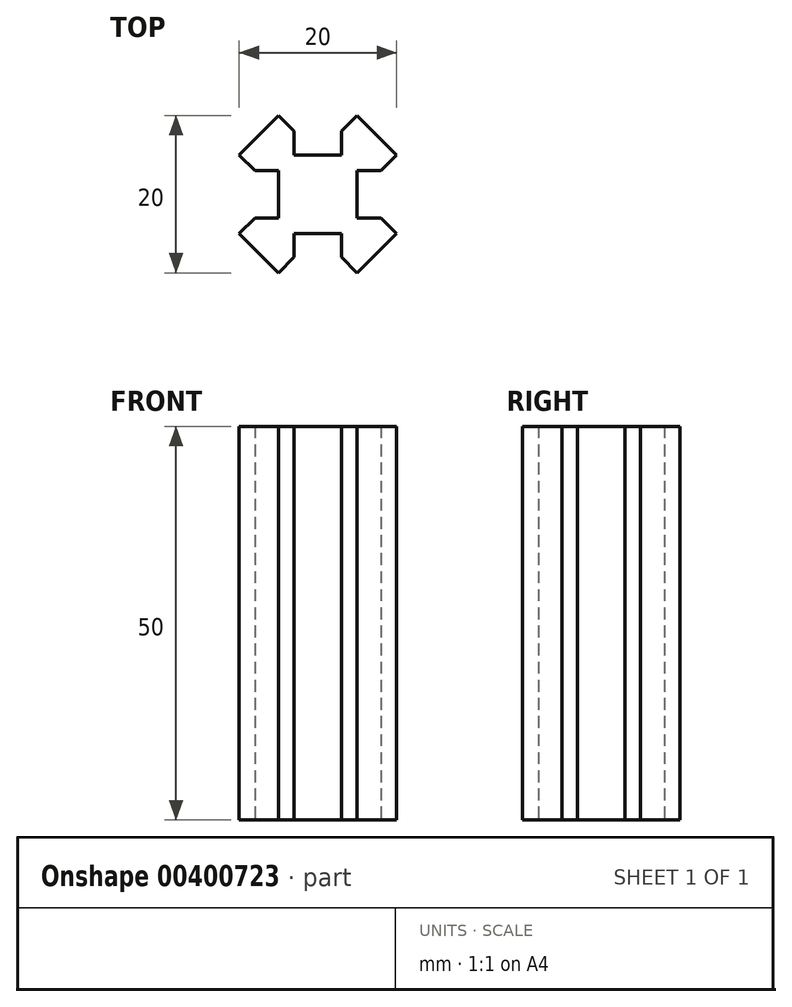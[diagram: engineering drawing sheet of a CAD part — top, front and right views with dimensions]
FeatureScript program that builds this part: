
annotation { "Feature Type Name" : "Feature", "Feature Type Description" : "" }
export const myFeature = defineFeature(function(context is Context, id is Id, definition is map)
    precondition{}
    {
        {
            var Q0;
            Q0=qCreatedBy(makeId("Top.planeOp"),FACE);
            var sketch = newSketch(context, id + "F0", { "sketchPlane" : qUnion([Q0])});
            skLineSegment(sketch, "E0.bottom", {"start": v(10, 10) * mm, "end": v(-10, 10) * mm});
            skLineSegment(sketch, "E0.top", {"start": v(10, -10) * mm, "end": v(-10, -10) * mm});
            skLineSegment(sketch, "E0.left", {"start": v(10, 10) * mm, "end": v(10, -10) * mm});
            skLineSegment(sketch, "E0.right", {"start": v(-10, 10) * mm, "end": v(-10, -10) * mm});
            skPoint(sketch, "E0.middle", {"position": v(0, 0) * mm});
            skLineSegment(sketch, "E1.bottom", {"start": v(5, -5) * mm, "end": v(-5, -5) * mm});
            skLineSegment(sketch, "E1.top", {"start": v(5, 5) * mm, "end": v(-5, 5) * mm});
            skLineSegment(sketch, "E1.left", {"start": v(5, -5) * mm, "end": v(5, 5) * mm});
            skLineSegment(sketch, "E1.right", {"start": v(-5, -5) * mm, "end": v(-5, 5) * mm});
            skLineSegment(sketch, "E2", {"start": v(10, -10) * mm, "end": v(10, -5) * mm});
            skLineSegment(sketch, "E3", {"start": v(10, -10) * mm, "end": v(5, -10) * mm});
            skLineSegment(sketch, "E4", {"start": v(5, -10) * mm, "end": v(3, -8) * mm});
            skLineSegment(sketch, "E5", {"start": v(10, -5) * mm, "end": v(8, -3) * mm});
            skLineSegment(sketch, "E6.top", {"start": v(10, 10) * mm, "end": v(10, 5) * mm});
            skLineSegment(sketch, "E6.left", {"start": v(5, 10) * mm, "end": v(10, 10) * mm});
            skLineSegment(sketch, "E7", {"start": v(10, 10) * mm, "end": v(5, 10) * mm});
            skLineSegment(sketch, "E8", {"start": v(10, 5) * mm, "end": v(8, 3) * mm});
            skLineSegment(sketch, "E9", {"start": v(5, 10) * mm, "end": v(3, 8) * mm});
            skLineSegment(sketch, "E10.top", {"start": v(-10, -10) * mm, "end": v(-10, -5) * mm});
            skLineSegment(sketch, "E10.left", {"start": v(-5, -10) * mm, "end": v(-10, -10) * mm});
            skLineSegment(sketch, "E11", {"start": v(-10, -10) * mm, "end": v(-5, -10) * mm});
            skLineSegment(sketch, "E12", {"start": v(-10, -5) * mm, "end": v(-8, -3) * mm});
            skLineSegment(sketch, "E13", {"start": v(-5, -10) * mm, "end": v(-3, -8) * mm});
            skLineSegment(sketch, "E14.top", {"start": v(-10, 10) * mm, "end": v(-5, 10) * mm});
            skLineSegment(sketch, "E14.left", {"start": v(-10, 5) * mm, "end": v(-10, 10) * mm});
            skLineSegment(sketch, "E15", {"start": v(-10, 10) * mm, "end": v(-10, 5) * mm});
            skLineSegment(sketch, "E16", {"start": v(-5, 10) * mm, "end": v(-3, 8) * mm});
            skLineSegment(sketch, "E17", {"start": v(-10, 5) * mm, "end": v(-8, 3) * mm});
            skLineSegment(sketch, "E18", {"start": v(-10, 5) * mm, "end": v(-5, 10) * mm});
            skLineSegment(sketch, "E19", {"start": v(5, 10) * mm, "end": v(10, 5) * mm});
            skLineSegment(sketch, "E20", {"start": v(5, -10) * mm, "end": v(10, -5) * mm});
            skLineSegment(sketch, "E21", {"start": v(-10, -5) * mm, "end": v(-5, -10) * mm});
            skLineSegment(sketch, "E22", {"start": v(-8, -3) * mm, "end": v(-5, -3) * mm});
            skLineSegment(sketch, "E23", {"start": v(-8, 3) * mm, "end": v(-5, 3) * mm});
            skPoint(sketch, "E23.endSnap0", {"position": v(-5, 0) * mm});
            skLineSegment(sketch, "E24", {"start": v(-3, 8) * mm, "end": v(-3, 5) * mm});
            skLineSegment(sketch, "E25", {"start": v(3, 8) * mm, "end": v(3, 5) * mm});
            skLineSegment(sketch, "E26", {"start": v(8, 3) * mm, "end": v(5, 3) * mm});
            skLineSegment(sketch, "E27", {"start": v(8, -3) * mm, "end": v(5, -3) * mm});
            skLineSegment(sketch, "E28", {"start": v(3, -8) * mm, "end": v(3, -5) * mm});
            skLineSegment(sketch, "E29", {"start": v(-3, -8) * mm, "end": v(-3, -5) * mm});
            skSolve(sketch);
        }
        {
            var Q0;
            Q0=makeQuery(id+"F0.imprint","IMPRINT",FACE,{"disambiguationData":[TD([[makeQuery(id+"F0.imprint","IMPRINT",EDGE,{"derivedFrom":sQuery(id+"F0.wireOp",EDGE,"E16")}),-1.0]])]});
            var Q1;
            {var subQ1=sQuery(id+"F0.wireOp",EDGE,"E1.bottom");var subQ4=sQuery(id+"F0.wireOp",EDGE,"E1.left");var subQ9=makeQuery(id+"F0.imprint","INTERSECT",VERTEX,{"derivedFrom":[subQ1,subQ4]});Q1=makeQuery(id+"F0.imprint","IMPRINT",FACE,{"disambiguationData":[TD([[makeQuery(id+"F0.imprint","IMPRINT",EDGE,{"disambiguationData":[TD([[subQ9,-1.0]])],"derivedFrom":subQ1}),-1.0]])]});}
            var Q2;
            Q2=makeQuery(id+"F0.imprint","IMPRINT",FACE,{"disambiguationData":[TD([[makeQuery(id+"F0.imprint","IMPRINT",EDGE,{"derivedFrom":sQuery(id+"F0.wireOp",EDGE,"E8")}),-1.0]])]});
            var Q3;
            Q3=makeQuery(id+"F0.imprint","IMPRINT",FACE,{"disambiguationData":[TD([[makeQuery(id+"F0.imprint","IMPRINT",EDGE,{"derivedFrom":sQuery(id+"F0.wireOp",EDGE,"E4")}),-1.0]])]});
            var Q4;
            Q4=makeQuery(id+"F0.imprint","IMPRINT",FACE,{"disambiguationData":[TD([[makeQuery(id+"F0.imprint","IMPRINT",EDGE,{"derivedFrom":sQuery(id+"F0.wireOp",EDGE,"E12")}),-1.0]])]});
            extrude(context, id + "F1", {"entities" : qUnion([Q0, Q1, Q2, Q3, Q4]), "depth" : 50 * mm});
        }
    });
